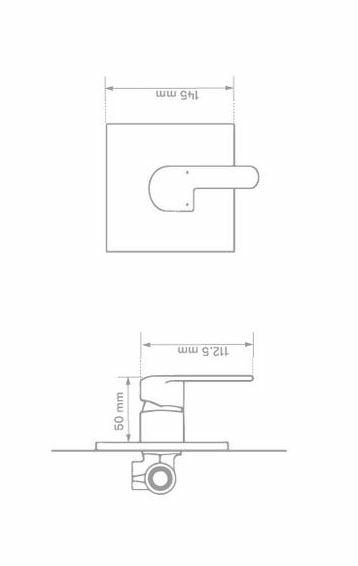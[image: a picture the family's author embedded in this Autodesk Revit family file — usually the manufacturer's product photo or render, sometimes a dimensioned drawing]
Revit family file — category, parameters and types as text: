
# Revit family: 01-1553-11-LLAVE MÓVIL PARED C CUERPO PIANA
name_source: partatom
category: Plumbing Fixtures
revit_build: Autodesk Revit 2018 (Build: 20170223_1515(x64)
units: mm (PartAtom-declared; Revit-internal decimal feet)

## family parameters
Cut with Voids When Loaded = No
Host = Face
OmniClass Number = 23.31.11.00
Part Type = Normal
Room Calculation Point = No
Round Connector Dimension = Use Diameter
Shared = No

## types (1)
- 01-1553-11
    Alto = 298 mm  [stored 0.97769 ft]
    Ancho = 75 mm  [stored 0.246063 ft]
    CW Connection = Yes
    Default Elevation = 0 mm  [stored 0 ft]
    Description = LLAVE MÓVIL PARED
    Finish = Plastico ABS Cromado
    HW Connection = Yes
    Largo = 260 mm
    Link Ficha Tecnica = http://infotecnica.gricol.com
    Manufacturer = Gricol
    Model = 01-1553-11
    Product Name = LLAVE MÓVIL PARED C CUERPO PLÁSTICO PIANA
    Type Image = LLAVE MÓVIL PARED C CUERPO PLÁSTICO PIANA PLANO.jpg
    URL = https://www.gricol.com
    Vent Connection = No
    Waste Connection = No

note: [stored X ft] marks values corroborated as IEEE doubles in the binary element streams (Revit-internal decimal feet)

## geometry (parser evidence)
native form markers: Blend x4, Sweep x5
no freeform markers — native parametric forms only
